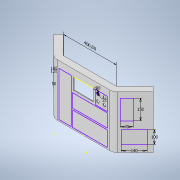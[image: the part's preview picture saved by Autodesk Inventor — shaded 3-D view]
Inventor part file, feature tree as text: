
AUTODESK INVENTOR PART (.ipt)
format: ipt  version: 2020 (Build 240168000, 168)  size: 194,560 bytes
history: native  units: mm
features: sketch x7, other x4, extrude x3, shell x1, pattern_linear x1, projected_geometry x1
ambient origin geometry x8: Origin, YZ Plane, XZ Plane, XY Plane, X Axis, Y Axis, Z Axis, Center Point
bodies: Solid1 (feature_tree)
feature tree (17):
  other  "Annotations"
  sketch  "Sketch1"  dims[d0=50.0mm d1=800.0mm d2=200.0mm]
  extrude  "Extrusion1"  Depth=50.0mm
  sketch  "Sketch4"  dims[d3=200.0mm d4=400.0mm d5=0.0mm]
  other  "Bend Part1"
  other  "Bend Part2"
  shell  "Shell1"  Thickness=200.0mm
  extrude  "Extrusion2"  Depth=400.0mm TaperAngle=0.0deg
  extrude  "Extrusion3"  Depth=200.0mm
  pattern_linear  "Rectangular Pattern1"  Count1=9  [1 undecoded]
  sketch  "Sketch7"  dims[d10=10.0mm d11=45.0deg]
  sketch  "Sketch8"  dims[d12=5.0mm d13=90.0mm]
  sketch  "Sketch9"  dims[d14=150.0mm d15=260.0mm d16=0.0mm d17=0.0mm d18=22.0mm d19=20.0mm d20=20.0mm d21=0.0mm d22=0.0mm d23=20.0mm d25=50.0mm d26=20.0mm d28=50.0mm d29=120.0mm d30=100.0mm d31=50.0mm d32=70.0mm d33=150.0mm d34=140.0mm d35=100.0mm d36=0.0mm d37=10.0mm d38=400.0mm]
  projected_geometry  "Projected Loop1"
  sketch  "Sketch5"  dims[d6=200.0mm d7=200.0mm]
  sketch  "Sketch6"  dims[d8=10.0mm d9=45.0deg]
  other  "Linear Dimension 1"
note: 1 required parameter value undecoded (feature->parameter linkage not recoverable at this tier; creation-order binding heuristic only, values carry confidence <= 0.55)
